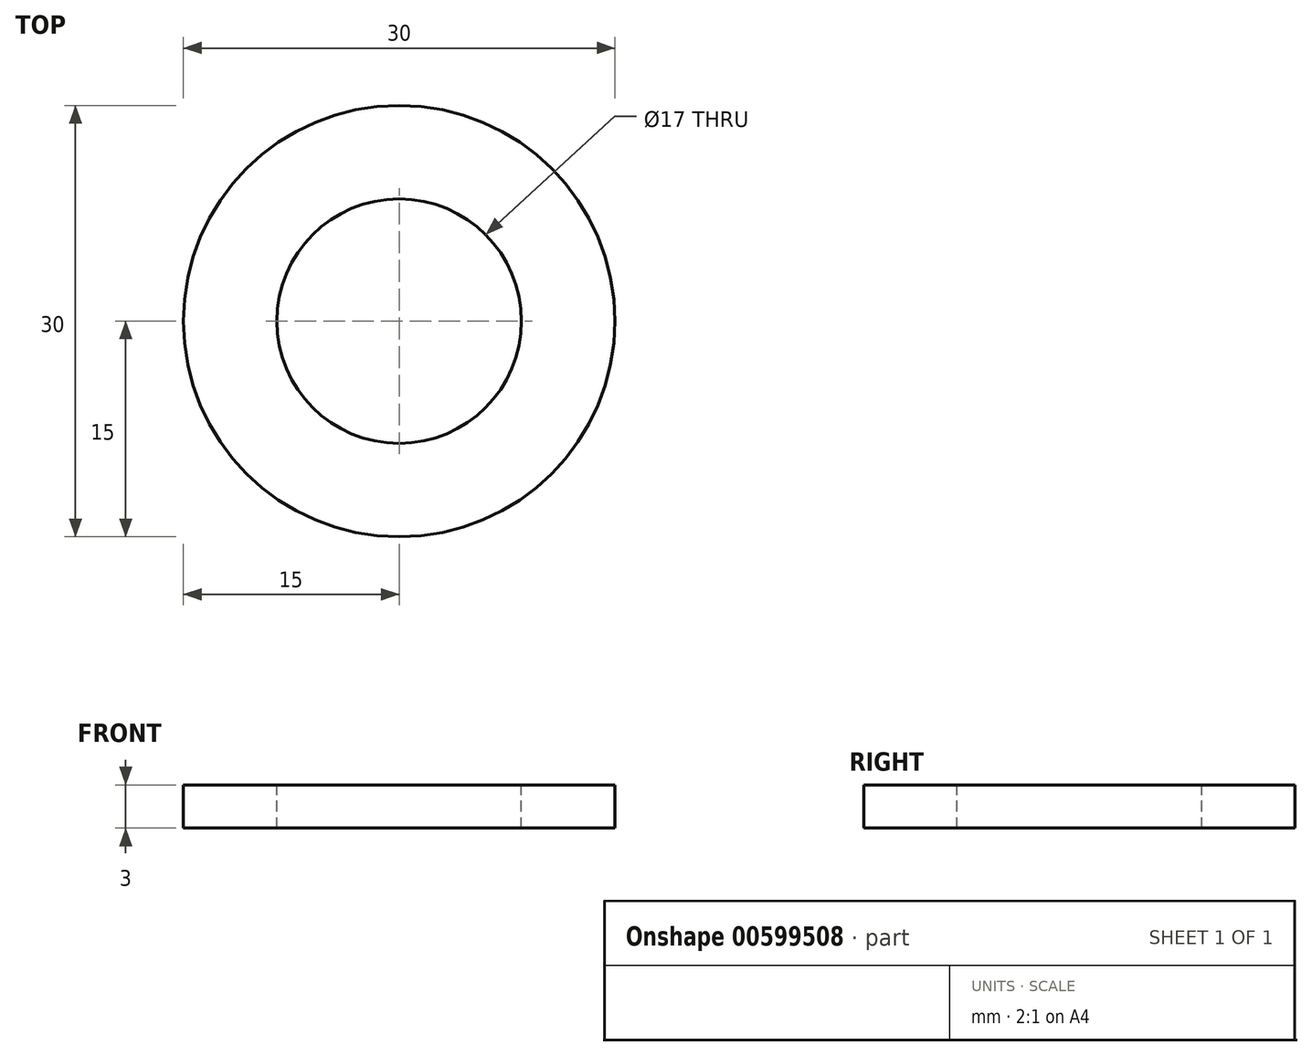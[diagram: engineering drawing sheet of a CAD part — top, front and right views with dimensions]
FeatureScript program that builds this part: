
annotation { "Feature Type Name" : "Feature", "Feature Type Description" : "" }
export const myFeature = defineFeature(function(context is Context, id is Id, definition is map)
    precondition{}
    {
        {
            var Q0;
            Q0=qCreatedBy(makeId("Front.planeOp"),FACE);
            var sketch = newSketch(context, id + "F0", { "sketchPlane" : qUnion([Q0])});
            skLineSegment(sketch, "E0", {"start": v(0, 6.68) * mm, "end": v(0, 0) * mm, "construction": true});
            skLineSegment(sketch, "E1", {"start": v(0, 0) * mm, "end": v(-15, 0) * mm, "construction": true});
            skLineSegment(sketch, "E2.bottom", {"start": v(-15, 0) * mm, "end": v(-8.5, 0) * mm});
            skLineSegment(sketch, "E2.top", {"start": v(-15, -3) * mm, "end": v(-8.5, -3) * mm});
            skLineSegment(sketch, "E2.left", {"start": v(-15, 0) * mm, "end": v(-15, -3) * mm});
            skLineSegment(sketch, "E2.right", {"start": v(-8.5, 0) * mm, "end": v(-8.5, -3) * mm});
            skSolve(sketch);
        }
        {
            var Q0;
            Q0 = qSketchRegion(id + "F0", true);
            var Q1;
            Q1=sQuery(id+"F0.wireOp",EDGE,"E0");
            revolve(context, id + "F1", {"entities" : qUnion([Q0]), "axis" : qUnion([Q1]), "revolveType" : RevolveType.FULL});
        }
    });
